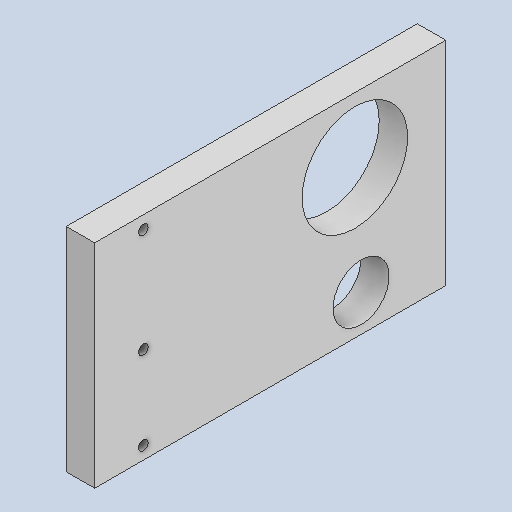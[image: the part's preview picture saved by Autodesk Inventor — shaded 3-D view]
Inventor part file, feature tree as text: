
AUTODESK INVENTOR PART (.ipt)
format: ipt  version: 2023 (Build 270158000, 158)  size: 227,328 bytes
history: native  units: in
note: dims shown in document units (in); Inventor stores cm internally (conversion verified against a paired STEP export)
features: extrude x1
ambient origin geometry x8: Origin, YZ Plane, XZ Plane, XY Plane, X Axis, Y Axis, Z Axis, Center Point
bodies: Body1 (feature_tree)
feature tree (1):
  extrude  "Extrusion6"  Depth=0.15in
